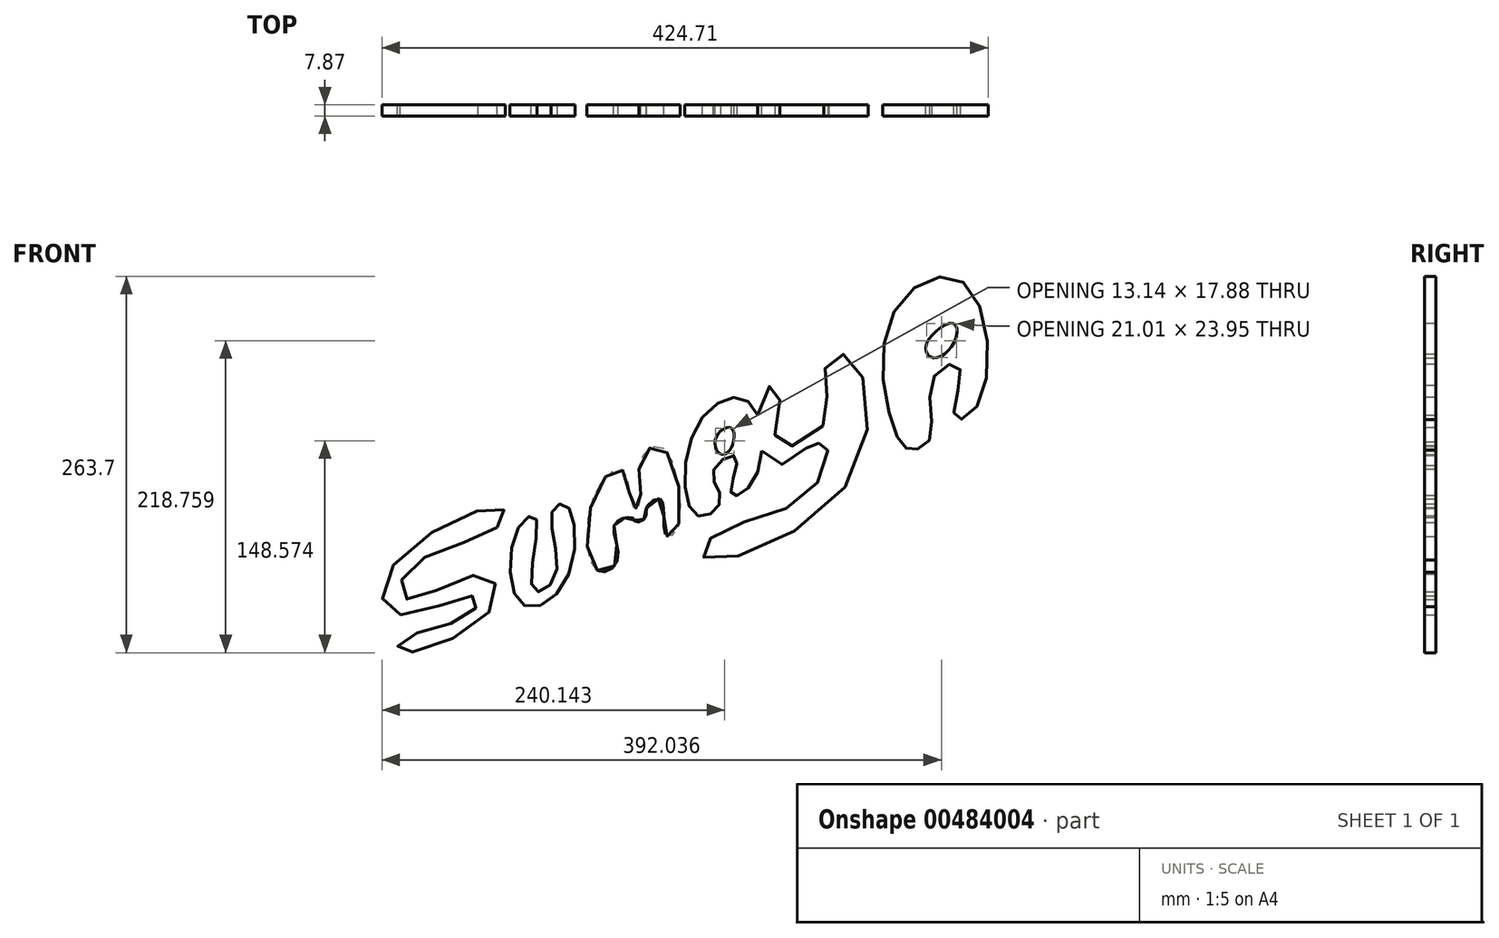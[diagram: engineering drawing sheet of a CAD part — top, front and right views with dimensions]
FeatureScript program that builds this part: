
annotation { "Feature Type Name" : "Feature", "Feature Type Description" : "" }
export const myFeature = defineFeature(function(context is Context, id is Id, definition is map)
    precondition{}
    {
        {
            var Q0;
            Q0=qCreatedBy(makeId("Front.planeOp"),FACE);
            var sketch = newSketch(context, id + "F0", { "sketchPlane" : qUnion([Q0])});
            skFitSpline(sketch, "E0", {"points": [v(-207.87, -31.64) * mm, v(-270.48, -61.14) * mm, v(-270.9, -81.95) * mm, v(-217.47, -64.63) * mm, v(-212.05, -89.03) * mm, v(-275.91, -118.8) * mm, v(-273.4, -109.95) * mm, v(-227.07, -92.57) * mm, v(-222.9, -80) * mm, v(-278.42, -92.58) * mm, v(-281.75, -59.9) * mm, v(-204.53, -18.4) * mm, v(-207.87, -31.64) * mm]});
            skFitSpline(sketch, "E1", {"points": [v(-192.85, -31.64) * mm, v(-191.18, -84.74) * mm, v(-160.29, -70.02) * mm, v(-159.45, -16.1) * mm, v(-169.47, -21.47) * mm, v(-166.97, -66.13) * mm, v(-182.4, -75.3) * mm, v(-180.74, -25.3) * mm, v(-192.85, -31.64) * mm]});
            skFitSpline(sketch, "E2", {"points": [v(-137.75, -62) * mm, v(-139, -7.68) * mm, v(-119.38, 7.9) * mm, v(-112.28, -17.82) * mm, v(-107.7, -15.17) * mm, v(-107.7, 13.4) * mm, v(-92.67, 24.88) * mm, v(-81.4, -31.64) * mm, v(-89.74, -36.92) * mm, v(-93.08, -12.2) * mm, v(-103.1, -17.57) * mm, v(-103.52, -24.29) * mm, v(-110.2, -27.99) * mm, v(-112.7, -25.26) * mm, v(-119.38, -25.35) * mm, v(-126.06, -31.64) * mm, v(-123.55, -54.9) * mm, v(-137.75, -62) * mm]});
            skFitSpline(sketch, "E3", {"points": [v(-67.62, -23.33) * mm, v(-68.46, 38.43) * mm, v(-31.72, 56.44) * mm, v(-28.38, 0.63) * mm, v(-43.83, -7.82) * mm, v(-40.49, 17.71) * mm, v(-56.35, 7.97) * mm, v(-51.34, -13.02) * mm, v(-67.62, -23.33) * mm]});
            skFitSpline(sketch, "E4", {"points": [v(-54.26, 31.8) * mm, v(-43.83, 37.9) * mm, v(-43.83, 23.69) * mm, v(-51.76, 20.03) * mm, v(-54.26, 31.8) * mm]});
            skFitSpline(sketch, "E5", {"points": [v(-10.44, 64.55) * mm, v(-11.27, 26.54) * mm, v(22.54, 43.08) * mm, v(21.29, 77.52) * mm, v(37.15, 89.07) * mm, v(39.65, 2.11) * mm, v(-62.61, -53) * mm, v(-54.26, -36.23) * mm, v(10.85, -7.82) * mm, v(22.54, 27.18) * mm, v(16.28, 26.94) * mm, v(10.02, 24.9) * mm, v(-15.44, 12.16) * mm, v(-21.29, 63.46) * mm, v(-10.44, 64.55) * mm]});
            skFitSpline(sketch, "E6", {"points": [v(72.63, 31.8) * mm, v(68.87, 116.86) * mm, v(118.96, 140.1) * mm, v(129.4, 54.94) * mm, v(112.7, 45.87) * mm, v(116.04, 80.8) * mm, v(98.1, 73.99) * mm, v(96, 31.8) * mm, v(83.07, 22.74) * mm, v(72.63, 31.8) * mm]});
            skFitSpline(sketch, "E7", {"points": [v(93.08, 97.15) * mm, v(111.87, 111.24) * mm, v(111.87, 97.14) * mm, v(97.26, 87.3) * mm, v(93.08, 97.15) * mm]});
            skSolve(sketch);
        }
        {
            var Q0;
            Q0 = qSketchRegion(id + "F0", true);
            extrude(context, id + "F1", {"entities" : qUnion([Q0]), "depth" : 7.87 * mm});
        }
    });
